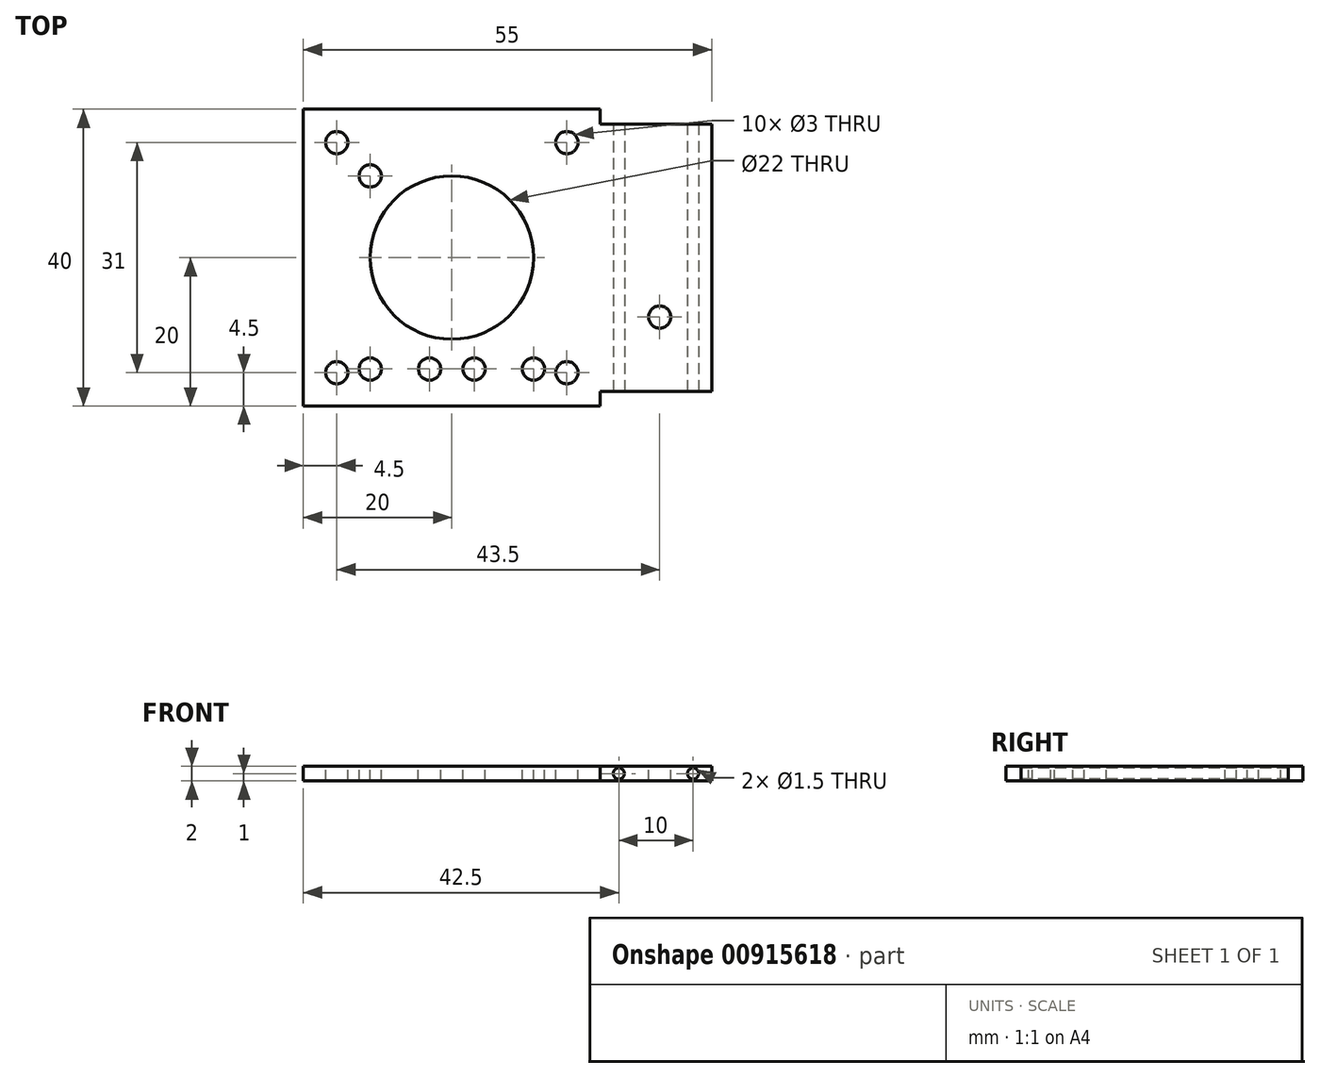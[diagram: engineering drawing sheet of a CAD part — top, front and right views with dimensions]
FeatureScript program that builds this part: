
annotation { "Feature Type Name" : "Feature", "Feature Type Description" : "" }
export const myFeature = defineFeature(function(context is Context, id is Id, definition is map)
    precondition{}
    {
        {
            var Q0;
            Q0=qCreatedBy(makeId("Top.planeOp"),FACE);
            var sketch = newSketch(context, id + "F0", { "sketchPlane" : qUnion([Q0])});
            skLineSegment(sketch, "E0.bottom", {"start": v(20, 20) * mm, "end": v(-20, 20) * mm});
            skLineSegment(sketch, "E0.top", {"start": v(20, -20) * mm, "end": v(-20, -20) * mm});
            skLineSegment(sketch, "E0.left", {"start": v(20, 20) * mm, "end": v(20, -20) * mm});
            skLineSegment(sketch, "E0.right", {"start": v(-20, 20) * mm, "end": v(-20, -20) * mm});
            skPoint(sketch, "E0.middle", {"position": v(0, 0) * mm});
            skSolve(sketch);
        }
        {
            var Q0;
            Q0=makeQuery(id+"F0.imprint","IMPRINT",FACE,{"disambiguationData":[TD([[makeQuery(id+"F0.imprint","IMPRINT",EDGE,{"derivedFrom":sQuery(id+"F0.wireOp",EDGE,"E0.bottom")}),1.0]])]});
            extrude(context, id + "F1", {"entities" : qUnion([Q0]), "depth" : 2 * mm, "offsetDistance" : 25 * mm});
        }
        {
            var Q0;
            Q0=makeQuery(id+"F1.opExtrude","SWEPT_FACE",FACE,{"disambiguationData":[OSD([sQuery(id+"F0.wireOp",EDGE,"E0.left")])]});
            var sketch = newSketch(context, id + "F2", { "sketchPlane" : qUnion([Q0])});
            skLineSegment(sketch, "E1.bottom", {"start": v(18, 2) * mm, "end": v(-18, 2) * mm});
            skLineSegment(sketch, "E1.top", {"start": v(18, 0) * mm, "end": v(-18, 0) * mm});
            skLineSegment(sketch, "E1.left", {"start": v(18, 2) * mm, "end": v(18, 0) * mm});
            skLineSegment(sketch, "E1.right", {"start": v(-18, 2) * mm, "end": v(-18, 0) * mm});
            skPoint(sketch, "E1.middle", {"position": v(0, 1) * mm});
            skPoint(sketch, "E1.middle.positionSnap0", {"position": v(20, 1) * mm});
            skPoint(sketch, "E1.middle.positionSnap1", {"position": v(0, 2) * mm});
            skPoint(sketch, "E1.centerSnap0", {"position": v(20, 1) * mm});
            skPoint(sketch, "E1.centerSnap1", {"position": v(0, 2) * mm});
            skSolve(sketch);
        }
        {
            var Q0;
            Q0=makeQuery(id+"F2.imprint","IMPRINT",FACE,{"disambiguationData":[TD([[makeQuery(id+"F2.imprint","IMPRINT",EDGE,{"derivedFrom":sQuery(id+"F2.wireOp",EDGE,"E1.bottom")}),1.0]])]});
            extrude(context, id + "F3", {"entities" : qUnion([Q0]), "operationType" : NewBodyOperationType.ADD, "depth" : 15 * mm, "offsetDistance" : 25 * mm});
        }
        {
            var Q0;
            Q0=makeQuery(id+"F1.opExtrude","CAP_FACE",FACE,{"disambiguationData":[OSD([sQuery(id+"F0.wireOp",EDGE,"E0.bottom"),sQuery(id+"F0.wireOp",EDGE,"E0.top"),sQuery(id+"F0.wireOp",EDGE,"E0.left"),sQuery(id+"F0.wireOp",EDGE,"E0.right")])],"isStart":false});
            var sketch = newSketch(context, id + "F4", { "sketchPlane" : qUnion([Q0])});
            skLineSegment(sketch, "E2", {"start": v(0, -20) * mm, "end": v(0, -15) * mm});
            skLineSegment(sketch, "E3", {"start": v(0, -15) * mm, "end": v(3, -15) * mm});
            skLineSegment(sketch, "E4", {"start": v(3, -15) * mm, "end": v(11, -15) * mm});
            skLineSegment(sketch, "E5", {"start": v(0, -15) * mm, "end": v(-3, -15) * mm});
            skLineSegment(sketch, "E6", {"start": v(-3, -15) * mm, "end": v(-11, -15) * mm});
            skCircle(sketch, "E7", {"center": v(-11, -15) * mm, "radius": 7 * mm});
            skCircle(sketch, "E8", {"center": v(11, -15) * mm, "radius": 7 * mm});
            skCircle(sketch, "E9", {"center": v(0, 0) * mm, "radius": 11 * mm});
            skCircle(sketch, "E10", {"center": v(0, 0) * mm, "radius": 7 * mm});
            skCircle(sketch, "E11", {"center": v(-11, 11) * mm, "radius": 7 * mm});
            skCircle(sketch, "E12", {"center": v(28, -8) * mm, "radius": 7 * mm});
            skLineSegment(sketch, "E13.bottom", {"start": v(15.5, 15.5) * mm, "end": v(-15.5, 15.5) * mm});
            skLineSegment(sketch, "E13.top", {"start": v(15.5, -15.5) * mm, "end": v(-15.5, -15.5) * mm});
            skLineSegment(sketch, "E13.left", {"start": v(15.5, 15.5) * mm, "end": v(15.5, -15.5) * mm});
            skLineSegment(sketch, "E13.right", {"start": v(-15.5, 15.5) * mm, "end": v(-15.5, -15.5) * mm});
            skSolve(sketch);
        }
        {
            var Q0;
            Q0=sQuery(id+"F4.wireOp",VERTEX,"E6.end");
            var Q1;
            Q1=sQuery(id+"F4.wireOp",VERTEX,"E4.end");
            var Q2;
            Q2=sQuery(id+"F4.wireOp",VERTEX,"E12.center");
            var Q3;
            Q3=sQuery(id+"F4.wireOp",VERTEX,"E11.center");
            var Q4;
            Q4=sQuery(id+"F4.wireOp",VERTEX,"E5.end");
            var Q5;
            Q5=sQuery(id+"F4.wireOp",VERTEX,"E3.end");
            var Q6;
            Q6=sQuery(id+"F4.wireOp",VERTEX,"E13.bottom.start");
            var Q7;
            Q7=sQuery(id+"F4.wireOp",VERTEX,"E13.bottom.end");
            var Q8;
            Q8=sQuery(id+"F4.wireOp",VERTEX,"E13.top.end");
            var Q9;
            Q9=sQuery(id+"F4.wireOp",VERTEX,"E13.top.start");
            var Q10;
            Q10=makeQuery(id+"F1.opExtrude","SWEPT_BODY",BODY,{"disambiguationData":[OSD([sQuery(id+"F0.wireOp",EDGE,"E0.bottom"),sQuery(id+"F0.wireOp",EDGE,"E0.top"),sQuery(id+"F0.wireOp",EDGE,"E0.left"),sQuery(id+"F0.wireOp",EDGE,"E0.right")])]});
            hole(context, id + "F5", {"style" : HoleStyle.SIMPLE, "endStyle" : HoleEndStyle.BLIND, "holeDiameter" : 3 * mm, "majorDiameter" : 5 * mm, "holeDepth" : 18 * mm, "isTappedThrough" : true, "tappedDepth" : 12 * mm, "tapClearance" : 3, "locations" : qUnion([Q0, Q1, Q2, Q3, Q4, Q5, Q6, Q7, Q8, Q9]), "scope" : qUnion([Q10])});
        }
        {
            var Q0;
            Q0=makeQuery(id+"F4.imprint","IMPRINT",FACE,{"disambiguationData":[TD([[makeQuery(id+"F4.imprint","IMPRINT",EDGE,{"derivedFrom":sQuery(id+"F4.wireOp",EDGE,"E10")}),-1.0]])]});
            var Q1;
            Q1=makeQuery(id+"F4.imprint","IMPRINT",FACE,{"disambiguationData":[TD([[makeQuery(id+"F4.imprint","IMPRINT",EDGE,{"derivedFrom":sQuery(id+"F4.wireOp",EDGE,"E10")}),1.0]])]});
            var Q2;
            {var subQ0=sQuery(id+"F4.wireOp",EDGE,"E11");var subQ1=sQuery(id+"F4.wireOp",EDGE,"E9");var subQ2=makeQuery(id+"F4.imprint","INTERSECT",VERTEX,{"disambiguationData":[OD(0.0)],"derivedFrom":[subQ1,subQ0]});Q2=makeQuery(id+"F4.imprint","IMPRINT",FACE,{"disambiguationData":[TD([[makeQuery(id+"F4.imprint","IMPRINT",EDGE,{"disambiguationData":[TD([[subQ2,1.0]])],"derivedFrom":subQ1}),1.0]])]});}
            extrude(context, id + "F6", {"entities" : qUnion([Q0, Q1, Q2]), "operationType" : NewBodyOperationType.REMOVE, "oppositeDirection" : true, "depth" : 25 * mm, "offsetDistance" : 25 * mm});
        }
        {
            var Q0;
            Q0=makeQuery(id+"F3.opExtrude","SWEPT_FACE",FACE,{"disambiguationData":[OSD([sQuery(id+"F2.wireOp",EDGE,"E1.right")])]});
            var sketch = newSketch(context, id + "F7", { "sketchPlane" : qUnion([Q0])});
            skLineSegment(sketch, "E14", {"start": v(32.5, 1) * mm, "end": v(22.5, 1) * mm});
            skPoint(sketch, "E14.startSnap0", {"position": v(35, 1) * mm});
            skSolve(sketch);
        }
        {
            var Q0;
            Q0=sQuery(id+"F7.wireOp",VERTEX,"E14.end");
            var Q1;
            Q1=sQuery(id+"F7.wireOp",VERTEX,"E14.start");
            var Q2;
            Q2=makeQuery(id+"F1.opExtrude","SWEPT_BODY",BODY,{"disambiguationData":[OSD([sQuery(id+"F0.wireOp",EDGE,"E0.bottom"),sQuery(id+"F0.wireOp",EDGE,"E0.top"),sQuery(id+"F0.wireOp",EDGE,"E0.left"),sQuery(id+"F0.wireOp",EDGE,"E0.right")])]});
            hole(context, id + "F8", {"style" : HoleStyle.SIMPLE, "endStyle" : HoleEndStyle.BLIND, "holeDiameter" : 1.5 * mm, "majorDiameter" : 5 * mm, "holeDepth" : 50 * mm, "isTappedThrough" : true, "tappedDepth" : 12 * mm, "tapClearance" : 3, "locations" : qUnion([Q0, Q1]), "scope" : qUnion([Q2])});
        }
    });
